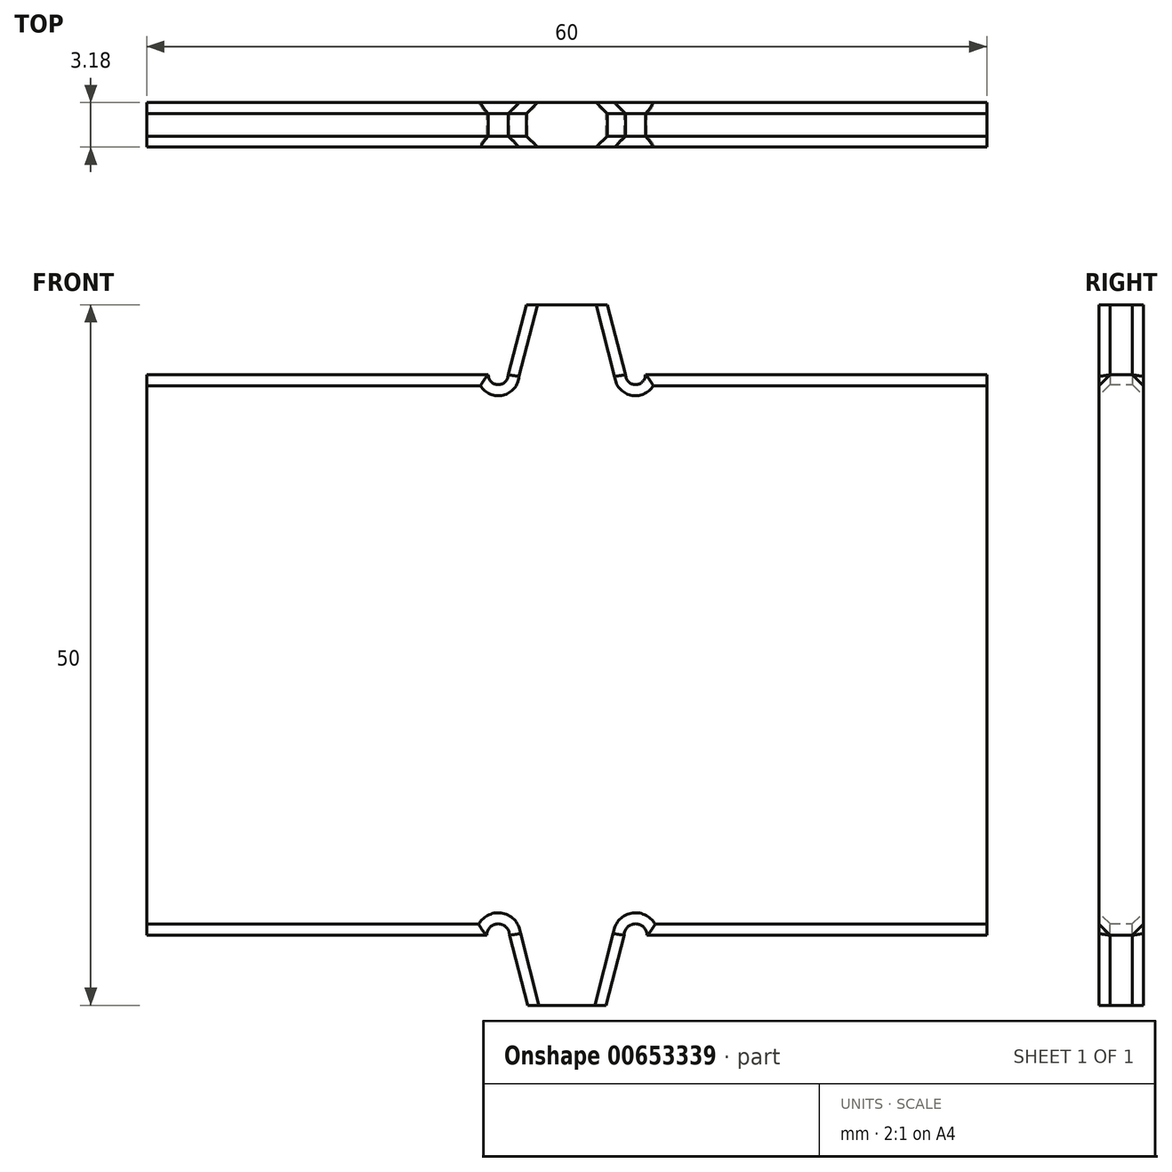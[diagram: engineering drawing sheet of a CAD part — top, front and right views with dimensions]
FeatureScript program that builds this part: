
annotation { "Feature Type Name" : "Feature", "Feature Type Description" : "" }
export const myFeature = defineFeature(function(context is Context, id is Id, definition is map)
    precondition{}
    {
        {
            var Q0;
            Q0=qCreatedBy(makeId("Front.planeOp"),FACE);
            var sketch = newSketch(context, id + "F0", { "sketchPlane" : qUnion([Q0])});
            skLineSegment(sketch, "E0.bottom", {"start": v(-30, -20.29) * mm, "end": v(-5.72, -20.29) * mm});
            skLineSegment(sketch, "E0.top", {"start": v(-30, 19.71) * mm, "end": v(-5.6, 19.71) * mm});
            skLineSegment(sketch, "E0.left", {"start": v(-30, -20.29) * mm, "end": v(-30, 19.71) * mm});
            skLineSegment(sketch, "E0.right", {"start": v(30, -19.71) * mm, "end": v(30, 19.71) * mm});
            skPoint(sketch, "E0.middle", {"position": v(0, 0) * mm});
            skLineSegment(sketch, "E1.MirrorCS", {"start": v(-2.8, -25.29) * mm, "end": v(-4.1, -20.29) * mm});
            skLineSegment(sketch, "E2", {"start": v(30, -19.71) * mm, "end": v(30, -20.29) * mm});
            skLineSegment(sketch, "E3", {"start": v(-2.9, 24.71) * mm, "end": v(-4.2, 19.71) * mm});
            skLineSegment(sketch, "E4.MirrorCS", {"start": v(30, -20.29) * mm, "end": v(30, 19.71) * mm});
            skLineSegment(sketch, "E5.MirrorCS", {"start": v(2.9, 24.71) * mm, "end": v(4.2, 19.71) * mm});
            skLineSegment(sketch, "E6.MirrorCS", {"start": v(30, 19.71) * mm, "end": v(5.6, 19.71) * mm});
            skPoint(sketch, "E7", {"position": v(-4.2, 19.73) * mm});
            skPoint(sketch, "E8", {"position": v(4.2, 19.71) * mm});
            skPoint(sketch, "E9", {"position": v(-4.1, -20.29) * mm});
            skPoint(sketch, "E10.orphan", {"position": v(6.05, 19.71) * mm});
            skPoint(sketch, "E11.orphan", {"position": v(-6.05, 19.71) * mm});
            skArc(sketch, "E12", {"start": v(4.2, 19.71) * mm, "mid": v(4.9, 19) * mm, "end": v(5.6, 19.71) * mm});
            skArc(sketch, "E13.MirrorCS", {"start": v(-4.2, 19.71) * mm, "mid": v(-4.9, 19) * mm, "end": v(-5.6, 19.71) * mm});
            skLineSegment(sketch, "E14.trimOffspring", {"start": v(5.72, -20.29) * mm, "end": v(30, -20.29) * mm});
            skLineSegment(sketch, "E15", {"start": v(-2.9, 24.71) * mm, "end": v(2.9, 24.71) * mm});
            skLineSegment(sketch, "E16.MirrorCS", {"start": v(2.8, -25.29) * mm, "end": v(4.1, -20.29) * mm});
            skArc(sketch, "E17", {"start": v(-4.1, -20.29) * mm, "mid": v(-4.9, -19.47) * mm, "end": v(-5.72, -20.29) * mm});
            skArc(sketch, "E18.MirrorCS", {"start": v(4.1, -20.29) * mm, "mid": v(4.9, -19.47) * mm, "end": v(5.72, -20.29) * mm});
            skLineSegment(sketch, "E19", {"start": v(-2.8, -25.29) * mm, "end": v(2.8, -25.29) * mm});
            skSolve(sketch);
        }
        {
            var Q0;
            Q0 = qSketchRegion(id + "F0", true);
            extrude(context, id + "F1", {"entities" : qUnion([Q0]), "depth" : 3.17 * mm, "offsetDistance" : 25.4 * mm});
        }
        {
            var Q0;
            Q0=makeQuery(id+"F1.opExtrude","CAP_EDGE",EDGE,{"disambiguationData":[OSD([sQuery(id+"F0.wireOp",EDGE,"E0.bottom")])],"isStart":true});
            var Q1;
            Q1=makeQuery(id+"F1.opExtrude","CAP_EDGE",EDGE,{"disambiguationData":[OSD([sQuery(id+"F0.wireOp",EDGE,"E14.trimOffspring")])],"isStart":true});
            var Q2;
            Q2=makeQuery(id+"F1.opExtrude","CAP_EDGE",EDGE,{"disambiguationData":[OSD([sQuery(id+"F0.wireOp",EDGE,"E14.trimOffspring")])],"isStart":false});
            var Q3;
            Q3=makeQuery(id+"F1.opExtrude","CAP_EDGE",EDGE,{"disambiguationData":[OSD([sQuery(id+"F0.wireOp",EDGE,"E0.bottom")])],"isStart":false});
            chamfer(context, id + "F2", {"entities" : qUnion([Q0, Q1, Q2, Q3]), "width" : 0.79 * mm, "tangentPropagation" : true});
        }
        {
            var Q0;
            Q0=makeQuery(id+"F1.opExtrude","CAP_EDGE",EDGE,{"disambiguationData":[OSD([sQuery(id+"F0.wireOp",EDGE,"E5.MirrorCS")])],"isStart":true});
            var Q1;
            Q1=makeQuery(id+"F1.opExtrude","CAP_EDGE",EDGE,{"disambiguationData":[OSD([sQuery(id+"F0.wireOp",EDGE,"E12")])],"isStart":true});
            var Q2;
            Q2=makeQuery(id+"F1.opExtrude","CAP_EDGE",EDGE,{"disambiguationData":[OSD([sQuery(id+"F0.wireOp",EDGE,"E3")])],"isStart":true});
            var Q3;
            Q3=makeQuery(id+"F1.opExtrude","CAP_EDGE",EDGE,{"disambiguationData":[OSD([sQuery(id+"F0.wireOp",EDGE,"E13.MirrorCS")])],"isStart":true});
            chamfer(context, id + "F3", {"entities" : qUnion([Q0, Q1, Q2, Q3]), "width" : 0.79 * mm, "tangentPropagation" : true});
        }
        {
            var Q0;
            Q0=makeQuery(id+"F1.opExtrude","CAP_EDGE",EDGE,{"disambiguationData":[OSD([sQuery(id+"F0.wireOp",EDGE,"E12")])],"isStart":false});
            var Q1;
            Q1=makeQuery(id+"F1.opExtrude","CAP_EDGE",EDGE,{"disambiguationData":[OSD([sQuery(id+"F0.wireOp",EDGE,"E5.MirrorCS")])],"isStart":false});
            var Q2;
            Q2=makeQuery(id+"F1.opExtrude","CAP_EDGE",EDGE,{"disambiguationData":[OSD([sQuery(id+"F0.wireOp",EDGE,"E3")])],"isStart":false});
            var Q3;
            Q3=makeQuery(id+"F1.opExtrude","CAP_EDGE",EDGE,{"disambiguationData":[OSD([sQuery(id+"F0.wireOp",EDGE,"E13.MirrorCS")])],"isStart":false});
            chamfer(context, id + "F4", {"entities" : qUnion([Q0, Q1, Q2, Q3]), "width" : 0.79 * mm, "tangentPropagation" : true});
        }
        {
            var Q0;
            Q0=makeQuery(id+"F1.opExtrude","CAP_EDGE",EDGE,{"disambiguationData":[OSD([sQuery(id+"F0.wireOp",EDGE,"E6.MirrorCS")])],"isStart":false});
            var Q1;
            Q1=makeQuery(id+"F1.opExtrude","CAP_EDGE",EDGE,{"disambiguationData":[OSD([sQuery(id+"F0.wireOp",EDGE,"E0.top")])],"isStart":false});
            var Q2;
            Q2=makeQuery(id+"F1.opExtrude","CAP_EDGE",EDGE,{"disambiguationData":[OSD([sQuery(id+"F0.wireOp",EDGE,"E6.MirrorCS")])],"isStart":true});
            var Q3;
            Q3=makeQuery(id+"F1.opExtrude","CAP_EDGE",EDGE,{"disambiguationData":[OSD([sQuery(id+"F0.wireOp",EDGE,"E0.top")])],"isStart":true});
            chamfer(context, id + "F5", {"entities" : qUnion([Q0, Q1, Q2, Q3]), "width" : 0.79 * mm, "tangentPropagation" : true});
        }
        {
            var Q0;
            Q0=makeQuery(id+"F1.opExtrude","CAP_EDGE",EDGE,{"disambiguationData":[OSD([sQuery(id+"F0.wireOp",EDGE,"E16.MirrorCS")])],"isStart":false});
            var Q1;
            Q1=makeQuery(id+"F1.opExtrude","CAP_EDGE",EDGE,{"disambiguationData":[OSD([sQuery(id+"F0.wireOp",EDGE,"E18.MirrorCS")])],"isStart":false});
            var Q2;
            Q2=makeQuery(id+"F1.opExtrude","CAP_EDGE",EDGE,{"disambiguationData":[OSD([sQuery(id+"F0.wireOp",EDGE,"E1.MirrorCS")])],"isStart":false});
            var Q3;
            Q3=makeQuery(id+"F1.opExtrude","CAP_EDGE",EDGE,{"disambiguationData":[OSD([sQuery(id+"F0.wireOp",EDGE,"E17")])],"isStart":false});
            chamfer(context, id + "F6", {"entities" : qUnion([Q0, Q1, Q2, Q3]), "width" : 0.79 * mm, "tangentPropagation" : true});
        }
        {
            var Q0;
            Q0=makeQuery(id+"F1.opExtrude","CAP_EDGE",EDGE,{"disambiguationData":[OSD([sQuery(id+"F0.wireOp",EDGE,"E16.MirrorCS")])],"isStart":true});
            var Q1;
            Q1=makeQuery(id+"F1.opExtrude","CAP_EDGE",EDGE,{"disambiguationData":[OSD([sQuery(id+"F0.wireOp",EDGE,"E18.MirrorCS")])],"isStart":true});
            var Q2;
            Q2=makeQuery(id+"F1.opExtrude","CAP_EDGE",EDGE,{"disambiguationData":[OSD([sQuery(id+"F0.wireOp",EDGE,"E1.MirrorCS")])],"isStart":true});
            var Q3;
            Q3=makeQuery(id+"F1.opExtrude","CAP_EDGE",EDGE,{"disambiguationData":[OSD([sQuery(id+"F0.wireOp",EDGE,"E17")])],"isStart":true});
            chamfer(context, id + "F7", {"entities" : qUnion([Q0, Q1, Q2, Q3]), "width" : 0.79 * mm, "tangentPropagation" : true});
        }
    });
